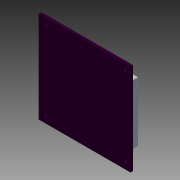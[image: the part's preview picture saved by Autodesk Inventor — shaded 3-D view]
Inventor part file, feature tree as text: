
AUTODESK INVENTOR PART (.ipt)
format: ipt  version: 2015 (Build 190159000, 159)  size: 132,608 bytes
history: native  units: in
note: dims shown in document units (in); Inventor stores cm internally (conversion verified against a paired STEP export)
features: extrude x2, sketch x2
ambient origin geometry x8: Origin, YZ Plane, XZ Plane, XY Plane, X Axis, Y Axis, Z Axis, Center Point
bodies: Solid1 (feature_tree)
feature tree (4):
  extrude  "Extrusion1"  Depth=2.25in
  extrude  "Extrusion4"  Depth=1.4567in
  sketch  "Sketch1"  dims[d0=0.0646in d1=0.0in d2=2.25in]
  sketch  "Sketch4"  dims[d4=2.25in d21=1.4567in d22=0.248in d23=0.0787in d24=0.1969in d25=0.0in d26=0.1024in d27=0.15in]
